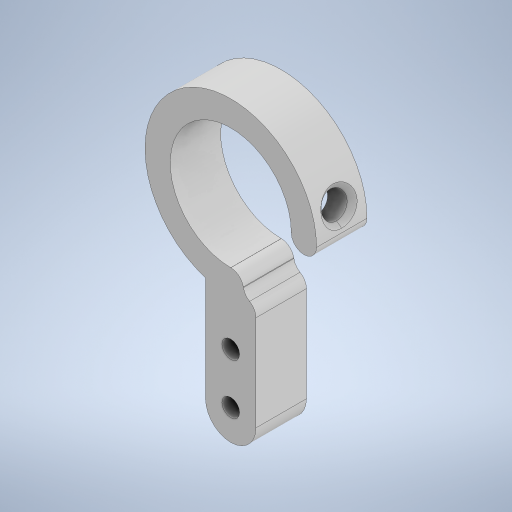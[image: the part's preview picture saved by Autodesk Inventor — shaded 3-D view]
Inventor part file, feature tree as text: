
AUTODESK INVENTOR PART (.ipt)
format: ipt  version: 2023.1 (Build 271208000, 208)  size: 328,192 bytes
history: native  units: mm
features: sketch x4, extrude x3, fillet x2, other x1, revolve x1, chamfer x1
ambient origin geometry x8: Origin, YZ Plane, XZ Plane, XY Plane, X Axis, Y Axis, Z Axis, Center Point
bodies: Body1 (feature_tree)
feature tree (12):
  other  "솔리드1"
  extrude  "돌출1"  Depth=10.0mm
  fillet  "모깎기1"  Radius=30.0mm
  revolve  "회전1"
  chamfer  "모따기1"  Distance=24.0mm
  extrude  "돌출2"  Depth=34.0mm
  fillet  "모깎기2"  Radius=10.0mm
  extrude  "돌출4"  Depth=2.5mm
  sketch  "스케치1"
  sketch  "스케치2"
  sketch  "스케치3"
  sketch  "스케치5"
